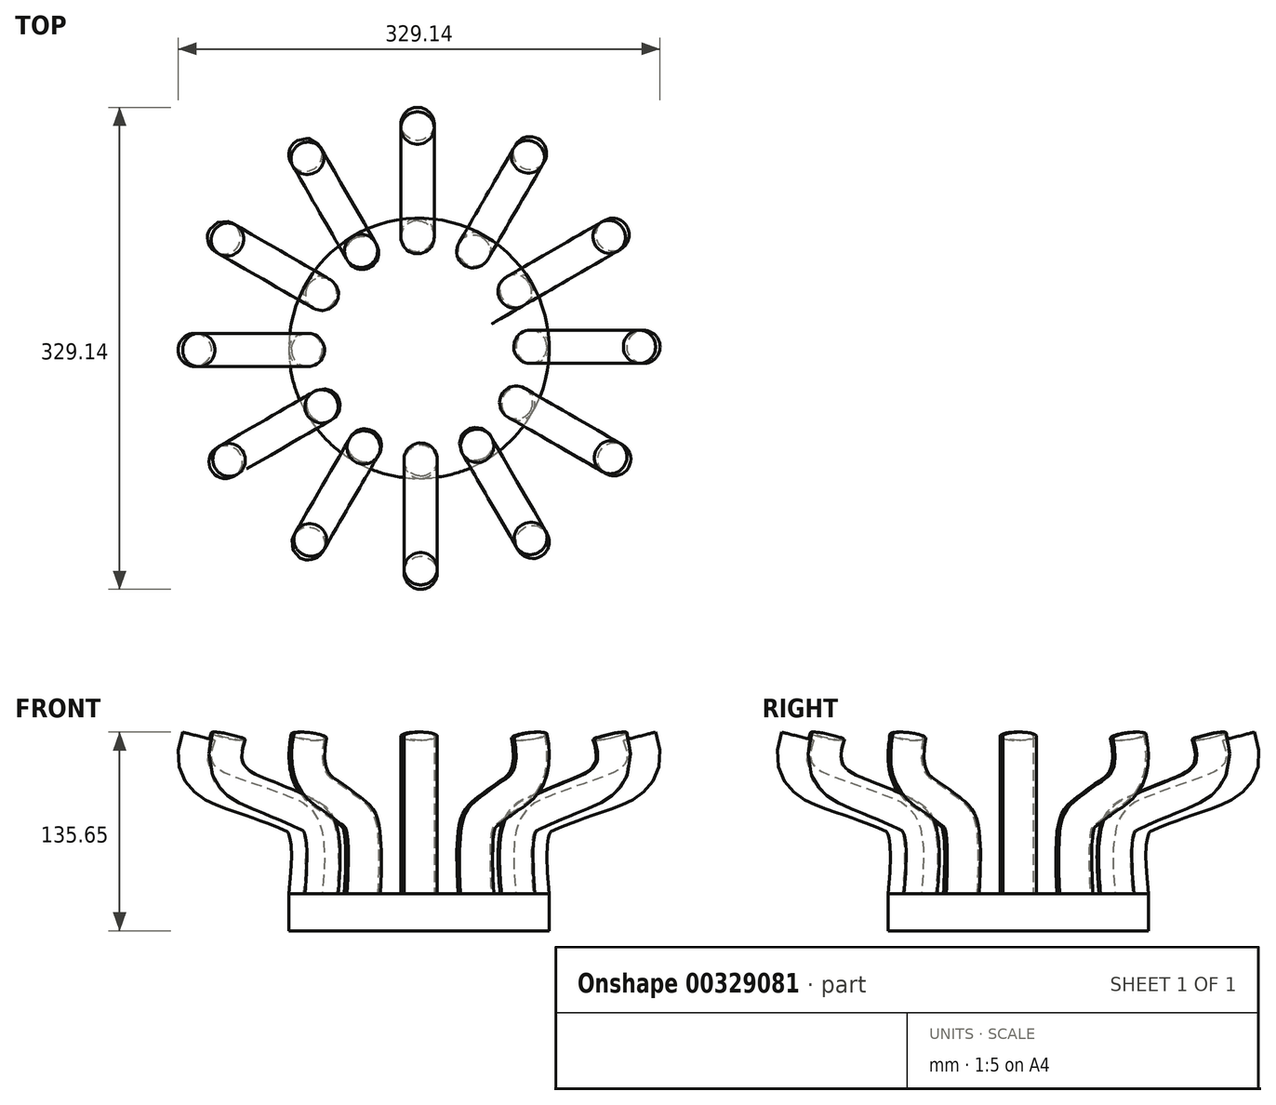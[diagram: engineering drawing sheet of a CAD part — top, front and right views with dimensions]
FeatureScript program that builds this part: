
annotation { "Feature Type Name" : "Feature", "Feature Type Description" : "" }
export const myFeature = defineFeature(function(context is Context, id is Id, definition is map)
    precondition{}
    {
        {
            var Q0;
            Q0=qCreatedBy(makeId("Top.planeOp"),FACE);
            var sketch = newSketch(context, id + "F0", { "sketchPlane" : qUnion([Q0])});
            skCircle(sketch, "E0", {"center": v(0, 0) * mm, "radius": 11.35 * mm});
            skSolve(sketch);
        }
        {
            var Q0;
            Q0=qCreatedBy(makeId("Front.planeOp"),FACE);
            var sketch = newSketch(context, id + "F1", { "sketchPlane" : qUnion([Q0])});
            skFitSpline(sketch, "E1", {"points": [v(0, 0) * mm, v(13.62, 55.16) * mm, v(44.83, 66.58) * mm, v(72.96, 107.46) * mm], "startDerivative": vector(-42.7, 386.15) * mm, "endDerivative": vector(-92.5, 246.67) * mm});
            skSolve(sketch);
        }
        {
            var Q0;
            Q0 = qSketchRegion(id + "F0", true);
            var Q1;
            Q1 = qConstructionFilter(qBodyType(qCreatedBy(id + "F1" ,EDGE), BodyType.WIRE), ConstructionObject.NO);
            sweep(context, id + "F2", {"profiles" : qUnion([Q0]), "path" : qUnion([Q1])});
        }
        {
            var Q0;
            Q0=makeQuery(id+"F2.opSweep","CAP_FACE",FACE,{"disambiguationData":[OSD([sQuery(id+"F0.wireOp",EDGE,"E0"),sQuery(id+"F1.wireOp",VERTEX,"E1.start")])],"isStart":true});
            var sketch = newSketch(context, id + "F3", { "sketchPlane" : qUnion([Q0])});
            skCircle(sketch, "E2", {"center": v(-77.53, 1.05) * mm, "radius": 88.89 * mm});
            skPoint(sketch, "E2.first.point", {"position": v(11.35, 0) * mm});
            skPoint(sketch, "E2.second.point", {"position": v(-166.4, 0) * mm});
            skPoint(sketch, "E2.third.point", {"position": v(-28.94, 75.49) * mm});
            skSolve(sketch);
        }
        {
            var Q0;
            {var subQ0=sQuery(id+"F3.wireOp",EDGE,"E2");var subQ1=makeQuery(id+"F2.opSweep","CAP_EDGE",EDGE,{"disambiguationData":[OSD([sQuery(id+"F0.wireOp",EDGE,"E0"),sQuery(id+"F1.wireOp",VERTEX,"E1.start")])],"isStart":true});var subQ2=makeQuery(id+"F3.imprint","INTERSECT",VERTEX,{"disambiguationData":[OD(0.0)],"derivedFrom":[subQ1,subQ0]});Q0=makeQuery(id+"F3.imprint","IMPRINT",FACE,{"disambiguationData":[TD([[makeQuery(id+"F3.imprint","IMPRINT",EDGE,{"disambiguationData":[TD([[subQ2,-1.0]])],"derivedFrom":subQ0}),1.0]])]});}
            var Q1;
            {var subQ0=sQuery(id+"F3.wireOp",EDGE,"E2");var subQ1=makeQuery(id+"F2.opSweep","CAP_EDGE",EDGE,{"disambiguationData":[OSD([sQuery(id+"F0.wireOp",EDGE,"E0"),sQuery(id+"F1.wireOp",VERTEX,"E1.start")])],"isStart":true});var subQ2=makeQuery(id+"F3.imprint","INTERSECT",VERTEX,{"disambiguationData":[OD(0.0)],"derivedFrom":[subQ1,subQ0]});Q1=makeQuery(id+"F3.imprint","IMPRINT",FACE,{"disambiguationData":[TD([[makeQuery(id+"F3.imprint","IMPRINT",EDGE,{"disambiguationData":[TD([[subQ2,1.0]])],"derivedFrom":subQ0}),1.0]])]});}
            extrude(context, id + "F4", {"entities" : qUnion([Q0, Q1]), "depth" : 25.4 * mm, "offsetDistance" : 25.4 * mm});
        }
        {
            var Q0;
            Q0=makeQuery(id+"F2.opSweep","SWEPT_BODY",BODY,{"disambiguationData":[OSD([sQuery(id+"F0.wireOp",EDGE,"E0"),sQuery(id+"F1.wireOp",EDGE,"E1")])]});
            var Q1;
            Q1=makeQuery(id+"F4.opExtrude","CAP_EDGE",EDGE,{"disambiguationData":[OSD([sQuery(id+"F3.wireOp",EDGE,"E2")])],"isStart":true});
            circularPattern(context, id + "F5", {"entities" : qUnion([Q0]), "axis" : qUnion([Q1]), "angle" : 360 * degree, "instanceCount" : 12, "equalSpace" : true});
        }
    });
